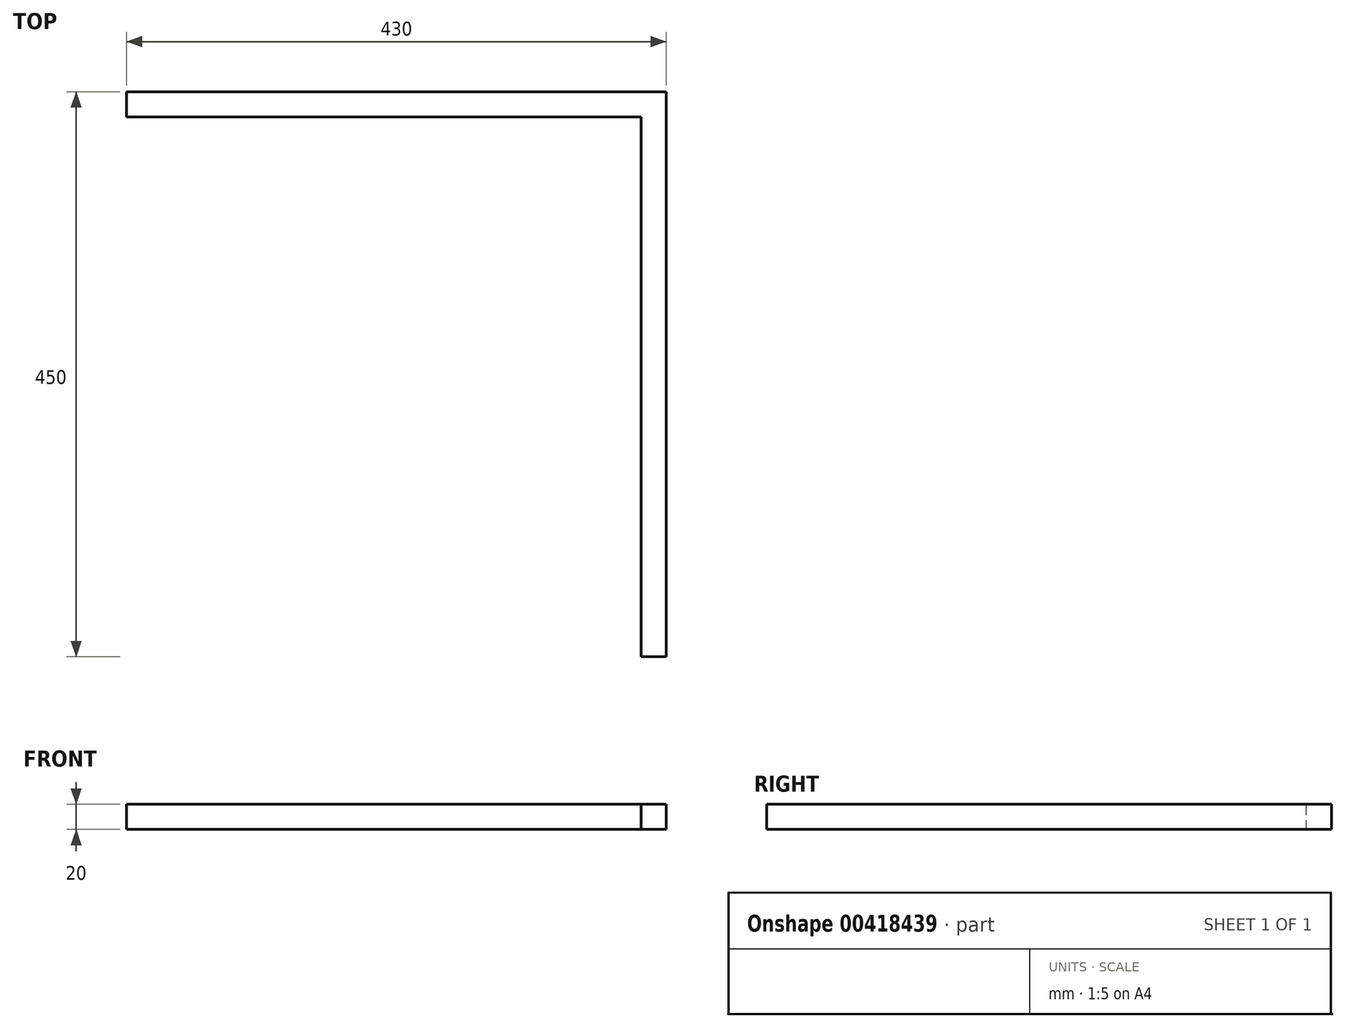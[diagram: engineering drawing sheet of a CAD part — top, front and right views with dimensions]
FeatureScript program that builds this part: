
annotation { "Feature Type Name" : "Feature", "Feature Type Description" : "" }
export const myFeature = defineFeature(function(context is Context, id is Id, definition is map)
    precondition{}
    {
        {
            var Q0;
            Q0=qCreatedBy(makeId("Front.planeOp"),FACE);
            var sketch = newSketch(context, id + "F0", { "sketchPlane" : qUnion([Q0])});
            skLineSegment(sketch, "E0.bottom", {"start": v(0, 0) * mm, "end": v(20, 0) * mm});
            skLineSegment(sketch, "E0.top", {"start": v(0, 20) * mm, "end": v(20, 20) * mm});
            skLineSegment(sketch, "E0.left", {"start": v(0, 0) * mm, "end": v(0, 20) * mm});
            skLineSegment(sketch, "E0.right", {"start": v(20, 0) * mm, "end": v(20, 20) * mm});
            skSolve(sketch);
        }
        {
            var Q0;
            Q0=makeQuery(id+"F0.imprint","IMPRINT",FACE,{"disambiguationData":[TD([[makeQuery(id+"F0.imprint","IMPRINT",EDGE,{"derivedFrom":sQuery(id+"F0.wireOp",EDGE,"E0.bottom")}),1.0]])]});
            extrude(context, id + "F1", {"entities" : qUnion([Q0]), "depth" : 450 * mm});
        }
        {
            var Q0;
            Q0=qCreatedBy(makeId("Right.planeOp"),FACE);
            var sketch = newSketch(context, id + "F2", { "sketchPlane" : qUnion([Q0])});
            skLineSegment(sketch, "E1.bottom", {"start": v(0, 0) * mm, "end": v(-20, 0) * mm});
            skLineSegment(sketch, "E1.top", {"start": v(0, 20) * mm, "end": v(-20, 20) * mm});
            skLineSegment(sketch, "E1.left", {"start": v(0, 0) * mm, "end": v(0, 20) * mm});
            skLineSegment(sketch, "E1.right", {"start": v(-20, 0) * mm, "end": v(-20, 20) * mm});
            skSolve(sketch);
        }
        {
            var Q0;
            Q0 = qSketchRegion(id + "F2", true);
            extrude(context, id + "F3", {"entities" : qUnion([Q0]), "operationType" : NewBodyOperationType.ADD, "oppositeDirection" : true, "depth" : 410 * mm});
        }
    });
